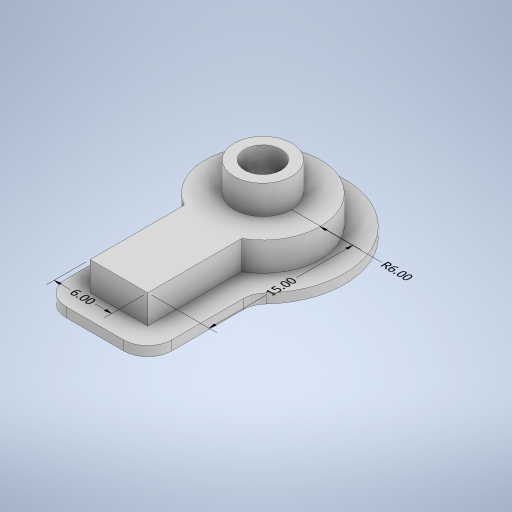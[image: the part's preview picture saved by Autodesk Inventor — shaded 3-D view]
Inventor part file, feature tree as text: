
AUTODESK INVENTOR PART (.ipt)
format: ipt  version: 2024.1 (Build 281209000, 209)  size: 324,096 bytes
history: native  units: mm
features: extrude x5, sketch x5, other x4, fillet x1, projected_geometry x1
ambient origin geometry x8: Origin, YZ Plane, XZ Plane, XY Plane, X Axis, Y Axis, Z Axis, Center Point
bodies: Body1 (feature_tree)
feature tree (16):
  other  "ソリッド1"
  extrude  "押し出し1"  Depth=12.0mm
  extrude  "押し出し2"  Depth=1.0mm TaperAngle=0.0deg
  extrude  "押し出し3"  Depth=6.0mm
  extrude  "押し出し4"  Depth=3.0mm TaperAngle=0.0deg
  extrude  "押し出し5"  Depth=3.8mm
  fillet  "フィレット1"  [1 undecoded]
  sketch  "スケッチ1"
  sketch  "スケッチ2"
  sketch  "スケッチ3"
  sketch  "スケッチ5"
  projected_geometry  "投影ループ1"
  sketch  "スケッチ6"
  other  "半径寸法 1"
  other  "長さ寸法 1"
  other  "長さ寸法 2"
note: 1 required parameter value undecoded (feature->parameter linkage not recoverable at this tier; creation-order binding heuristic only, values carry confidence <= 0.55)
